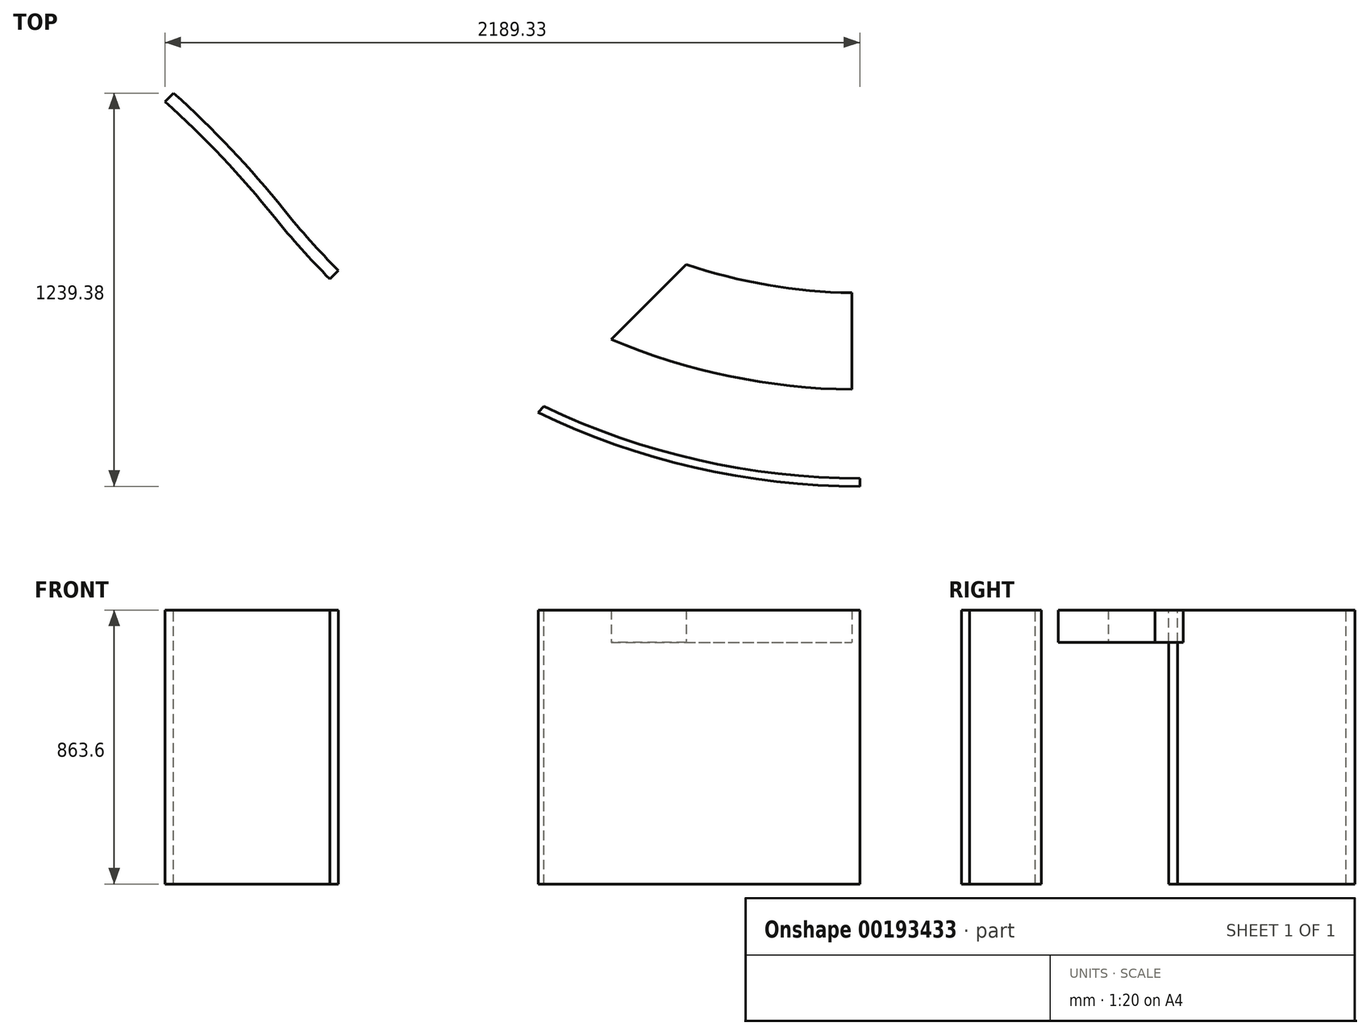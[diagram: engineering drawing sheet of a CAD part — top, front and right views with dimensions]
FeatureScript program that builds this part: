
annotation { "Feature Type Name" : "Feature", "Feature Type Description" : "" }
export const myFeature = defineFeature(function(context is Context, id is Id, definition is map)
    precondition{}
    {
        {
            var Q0;
            Q0=qCreatedBy(makeId("Top.planeOp"),FACE);
            var sketch = newSketch(context, id + "F0", { "sketchPlane" : qUnion([Q0])});
            skLineSegment(sketch, "E0", {"start": v(-2322.22, 117.32) * mm, "end": v(334.74, 117.32) * mm});
            skLineSegment(sketch, "E1", {"start": v(2049.24, -1597.18) * mm, "end": v(2049.24, -2206.78) * mm});
            skArc(sketch, "E2", {"start": v(2049.24, -1597.18) * mm, "mid": v(836.9, -1095.02) * mm, "end": v(334.74, 117.32) * mm});
            skArc(sketch, "E3.0", {"start": v(2049.24, -1901.98) * mm, "mid": v(1174.95, -1702.9) * mm, "end": v(473.05, -1144.9) * mm});
            skArc(sketch, "E4.0", {"start": v(2049.24, -2206.78) * mm, "mid": v(1042.98, -1977.65) * mm, "end": v(235.13, -1335.43) * mm});
            skLineSegment(sketch, "E5", {"start": v(-2322.22, 117.32) * mm, "end": v(-2341.09, -188.9) * mm});
            skPoint(sketch, "E6", {"position": v(-2322.22, 117.32) * mm});
            skArc(sketch, "E7", {"start": v(473.05, -1144.9) * mm, "mid": v(-773, -178.12) * mm, "end": v(-2322.22, 117.32) * mm});
            skArc(sketch, "E8.0", {"start": v(235.13, -1335.43) * mm, "mid": v(-913.65, -449.1) * mm, "end": v(-2341.09, -188.9) * mm});
            skPoint(sketch, "E9.orphan", {"position": v(-2400, -1144.9) * mm});
            skLineSegment(sketch, "E10.0", {"start": v(-2296.86, 115.77) * mm, "end": v(-2313.98, -162) * mm});
            skArc(sketch, "E11.0", {"start": v(254.96, -1319.55) * mm, "mid": v(-901.93, -426.51) * mm, "end": v(-2339.51, -163.36) * mm});
            skArc(sketch, "E12.0", {"start": v(2049.24, -2181.38) * mm, "mid": v(1053.98, -1954.75) * mm, "end": v(254.96, -1319.55) * mm});
            skLineSegment(sketch, "E13.0", {"start": v(2023.84, -1597) * mm, "end": v(2023.84, -2181.24) * mm});
            skLineSegment(sketch, "E14", {"start": v(2049.24, 117.32) * mm, "end": v(0, -1931.92) * mm});
            skLineSegment(sketch, "E15", {"start": v(-2339.51, -163.36) * mm, "end": v(-2322.22, 117.32) * mm});
            skLineSegment(sketch, "E16", {"start": v(-2339.51, -163.36) * mm, "end": v(-2313.98, -162) * mm});
            skLineSegment(sketch, "E17", {"start": v(-2296.86, 115.77) * mm, "end": v(-2322.22, 117.32) * mm});
            skLineSegment(sketch, "E18.bottom", {"start": v(2023.84, -1597) * mm, "end": v(2049.24, -1597) * mm});
            skLineSegment(sketch, "E18.top", {"start": v(2023.84, -1597.18) * mm, "end": v(2049.24, -1597.18) * mm});
            skLineSegment(sketch, "E18.left", {"start": v(2023.84, -1597) * mm, "end": v(2023.84, -1597.18) * mm});
            skLineSegment(sketch, "E18.right", {"start": v(2049.24, -1597) * mm, "end": v(2049.24, -1597.18) * mm});
            skLineSegment(sketch, "E19", {"start": v(2049.24, -2181.38) * mm, "end": v(2023.84, -2181.24) * mm});
            skLineSegment(sketch, "E20.MirrorCS", {"start": v(832.63, -1031.77) * mm, "end": v(1029.4, -1228.54) * mm});
            skLineSegment(sketch, "E21.0", {"start": v(424.4, -429.88) * mm, "end": v(-140.1, -994.38) * mm});
            skLineSegment(sketch, "E22.0", {"start": v(1502.04, -1507.51) * mm, "end": v(1007.02, -2002.53) * mm});
            skArc(sketch, "E23.0", {"start": v(205.4, -1359.24) * mm, "mid": v(40.22, -1169.65) * mm, "end": v(-140.1, -994.38) * mm});
            skArc(sketch, "E24.0", {"start": v(1007.02, -2002.53) * mm, "mid": v(570.8, -1725.02) * mm, "end": v(205.4, -1359.24) * mm});
            skPoint(sketch, "E25.orphan", {"position": v(-1077.63, -854.3) * mm});
            skSolve(sketch);
        }
        {
            var Q0;
            {var subQ0=sQuery(id+"F0.wireOp",EDGE,"E23.0");Q0=makeQuery(id+"F0.imprint","IMPRINT",FACE,{"disambiguationData":[TD([[makeQuery(id+"F0.imprint","IMPRINT",EDGE,{"derivedFrom":subQ0}),-1.0]])]});}
            var Q1;
            {var subQ0=sQuery(id+"F0.wireOp",EDGE,"E22.0");var subQ1=sQuery(id+"F0.wireOp",EDGE,"E4.0");var subQ2=makeQuery(id+"F0.imprint","INTERSECT",VERTEX,{"derivedFrom":[subQ1,subQ0]});Q1=makeQuery(id+"F0.imprint","IMPRINT",FACE,{"disambiguationData":[TD([[makeQuery(id+"F0.imprint","IMPRINT",EDGE,{"disambiguationData":[TD([[subQ2,-1.0]])],"derivedFrom":subQ1}),1.0]])]});}
            extrude(context, id + "F1", {"entities" : qUnion([Q0, Q1]), "oppositeDirection" : true, "depth" : 762 * mm});
        }
        {
            var Q0;
            {var subQ5=sQuery(id+"F0.wireOp",EDGE,"E7");var subQ6=sQuery(id+"F0.wireOp",EDGE,"E3.0");var subQ7=makeQuery(id+"F0.imprint","INTERSECT",VERTEX,{"derivedFrom":[subQ6,subQ5]});Q0=makeQuery(id+"F0.imprint","IMPRINT",FACE,{"disambiguationData":[TD([[makeQuery(id+"F0.imprint","IMPRINT",EDGE,{"disambiguationData":[TD([[subQ7,1.0]])],"derivedFrom":subQ6}),1.0]])]});}
            var Q1;
            {var subQ7=sQuery(id+"F0.wireOp",EDGE,"E8.0");var subQ8=sQuery(id+"F0.wireOp",EDGE,"E4.0");var subQ9=makeQuery(id+"F0.imprint","INTERSECT",VERTEX,{"derivedFrom":[subQ8,subQ7]});Q1=makeQuery(id+"F0.imprint","IMPRINT",FACE,{"disambiguationData":[TD([[makeQuery(id+"F0.imprint","IMPRINT",EDGE,{"disambiguationData":[TD([[subQ9,1.0]])],"derivedFrom":subQ8}),-1.0]])]});}
            var Q2;
            {var subQ9=sQuery(id+"F0.wireOp",EDGE,"E23.0");Q2=makeQuery(id+"F0.imprint","IMPRINT",FACE,{"disambiguationData":[TD([[makeQuery(id+"F0.imprint","IMPRINT",EDGE,{"derivedFrom":subQ9}),-1.0]])]});}
            var Q3;
            {var subQ0=sQuery(id+"F0.wireOp",EDGE,"E22.0");var subQ1=sQuery(id+"F0.wireOp",EDGE,"E3.0");var subQ2=makeQuery(id+"F0.imprint","INTERSECT",VERTEX,{"derivedFrom":[subQ1,subQ0]});Q3=makeQuery(id+"F0.imprint","IMPRINT",FACE,{"disambiguationData":[TD([[makeQuery(id+"F0.imprint","IMPRINT",EDGE,{"disambiguationData":[TD([[subQ2,-1.0]])],"derivedFrom":subQ1}),1.0]])]});}
            var Q4;
            {var subQ0=sQuery(id+"F0.wireOp",EDGE,"E22.0");var subQ1=sQuery(id+"F0.wireOp",EDGE,"E4.0");var subQ2=makeQuery(id+"F0.imprint","INTERSECT",VERTEX,{"derivedFrom":[subQ1,subQ0]});Q4=makeQuery(id+"F0.imprint","IMPRINT",FACE,{"disambiguationData":[TD([[makeQuery(id+"F0.imprint","IMPRINT",EDGE,{"disambiguationData":[TD([[subQ2,-1.0]])],"derivedFrom":subQ1}),-1.0]])]});}
            var Q5;
            {var subQ0=sQuery(id+"F0.wireOp",EDGE,"E22.0");var subQ1=sQuery(id+"F0.wireOp",EDGE,"E4.0");var subQ2=makeQuery(id+"F0.imprint","INTERSECT",VERTEX,{"derivedFrom":[subQ1,subQ0]});Q5=makeQuery(id+"F0.imprint","IMPRINT",FACE,{"disambiguationData":[TD([[makeQuery(id+"F0.imprint","IMPRINT",EDGE,{"disambiguationData":[TD([[subQ2,-1.0]])],"derivedFrom":subQ1}),1.0]])]});}
            extrude(context, id + "F2", {"entities" : qUnion([Q0, Q1, Q2, Q3, Q4, Q5]), "operationType" : NewBodyOperationType.ADD, "depth" : 101.6 * mm});
        }
    });
